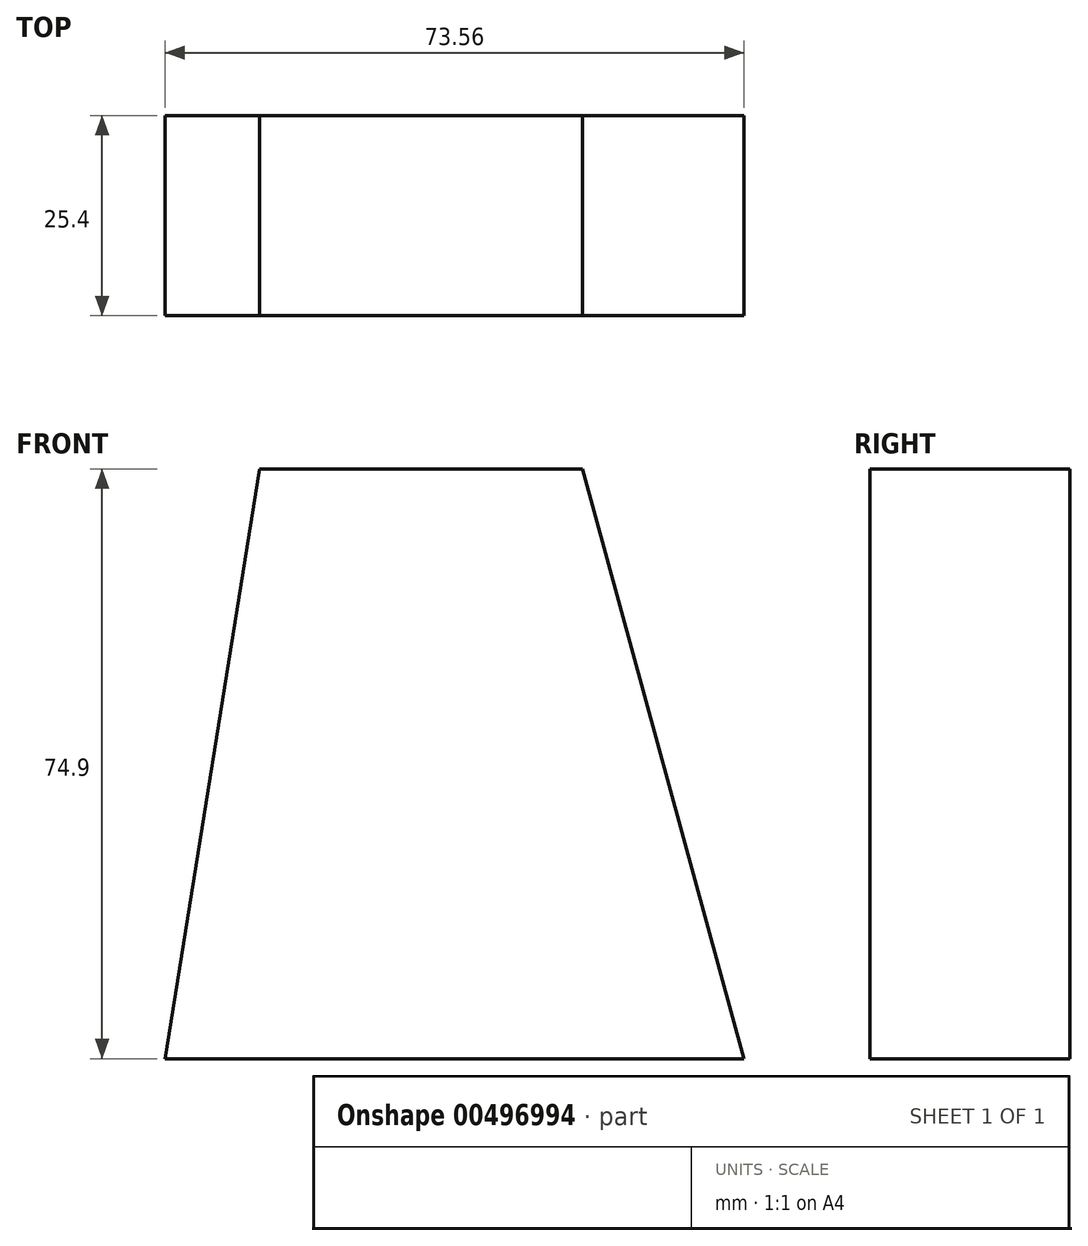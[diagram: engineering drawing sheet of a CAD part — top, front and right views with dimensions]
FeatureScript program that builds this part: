
annotation { "Feature Type Name" : "Feature", "Feature Type Description" : "" }
export const myFeature = defineFeature(function(context is Context, id is Id, definition is map)
    precondition{}
    {
        {
            var Q0;
            Q0=qCreatedBy(makeId("Front.planeOp"),FACE);
            var sketch = newSketch(context, id + "F0", { "sketchPlane" : qUnion([Q0])});
            skLineSegment(sketch, "E0", {"start": v(-46.37, -42.8) * mm, "end": v(-5.35, -42.8) * mm});
            skLineSegment(sketch, "E1", {"start": v(-5.35, -42.8) * mm, "end": v(-5.35, 32.1) * mm});
            skLineSegment(sketch, "E2", {"start": v(-5.35, 32.1) * mm, "end": v(-46.37, 32.1) * mm});
            skLineSegment(sketch, "E3", {"start": v(-46.37, 32.1) * mm, "end": v(-46.37, -42.8) * mm});
            skLineSegment(sketch, "E4", {"start": v(-5.35, -42.8) * mm, "end": v(6.69, -42.8) * mm});
            skLineSegment(sketch, "E5", {"start": v(-46.37, -42.8) * mm, "end": v(-58.4, -42.8) * mm});
            skLineSegment(sketch, "E6", {"start": v(-58.4, -42.8) * mm, "end": v(-46.37, 32.1) * mm});
            skLineSegment(sketch, "E7", {"start": v(6.69, -42.8) * mm, "end": v(15.16, -42.8) * mm});
            skLineSegment(sketch, "E8", {"start": v(15.16, -42.8) * mm, "end": v(-5.35, 32.1) * mm});
            skSolve(sketch);
        }
        {
            var Q0;
            Q0 = qSketchRegion(id + "F0", true);
            extrude(context, id + "F1", {"entities" : qUnion([Q0]), "depth" : 25.4 * mm});
        }
    });
